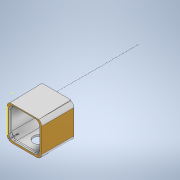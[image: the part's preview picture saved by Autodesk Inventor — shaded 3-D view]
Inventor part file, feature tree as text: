
AUTODESK INVENTOR PART (.ipt)
format: ipt  version: 2020 (Build 240168000, 168)  size: 298,496 bytes
history: native  units: in
note: dims shown in document units (in); Inventor stores cm internally (conversion verified against a paired STEP export)
features: sketch x7, extrude x6, projected_geometry x5, other x3, fillet x2, plane x1
ambient origin geometry x8: Origin, YZ Plane, XZ Plane, XY Plane, X Axis, Y Axis, Z Axis, Center Point
bodies: Solid1 (feature_tree)
feature tree (24):
  other  "Assembly4.iam"
  other  "Kauri modular session 5 mount.ipt:1"
  other  "session 5.ipt:1"
  extrude  "Extrusion1"  Depth=0.3937in TaperAngle=0.0deg
  extrude  "Extrusion2"  Depth=1.0in TaperAngle=0.0deg
  extrude  "Extrusion3"  Depth=0.3937in TaperAngle=0.0deg
  fillet  "Fillet1"  Radius=0.2362in
  fillet  "Fillet2"  Radius=0.0394in
  extrude  "Extrusion4"  Depth=0.3937in
  extrude  "Extrusion5"  Depth=0.0197in
  sketch  "Sketch6"  dims[d20=0.0197in d21=0.3937in d22=0.0in]
  plane  "Work Plane1"
  extrude  "Extrusion6"  Depth=0.3937in TaperAngle=0.0deg
  sketch  "Sketch1"  dims[d0=0.3937in d1=1.0in d2=0.0in]
  projected_geometry  "Projected Loop1"
  sketch  "Sketch2"  dims[d3=0.5906in d4=1.0in d5=0.0in]
  sketch  "Sketch3"  dims[d6=0.9843in d7=0.3937in d8=0.0in d9=0.2362in d10=0.0394in]
  projected_geometry  "Projected Loop2"
  sketch  "Sketch4"  dims[d12=0.0197in d15=0.3937in d16=0.0in d17=0.0197in]
  projected_geometry  "Projected Loop3"
  sketch  "Sketch5"  dims[d18=0.0197in d19=0.0197in]
  projected_geometry  "Projected Loop4"
  projected_geometry  "Projected Loop5"
  sketch  "Sketch7"  dims[d23=0.0in d24=0.0394in d25=1.378in d26=0.0in]
